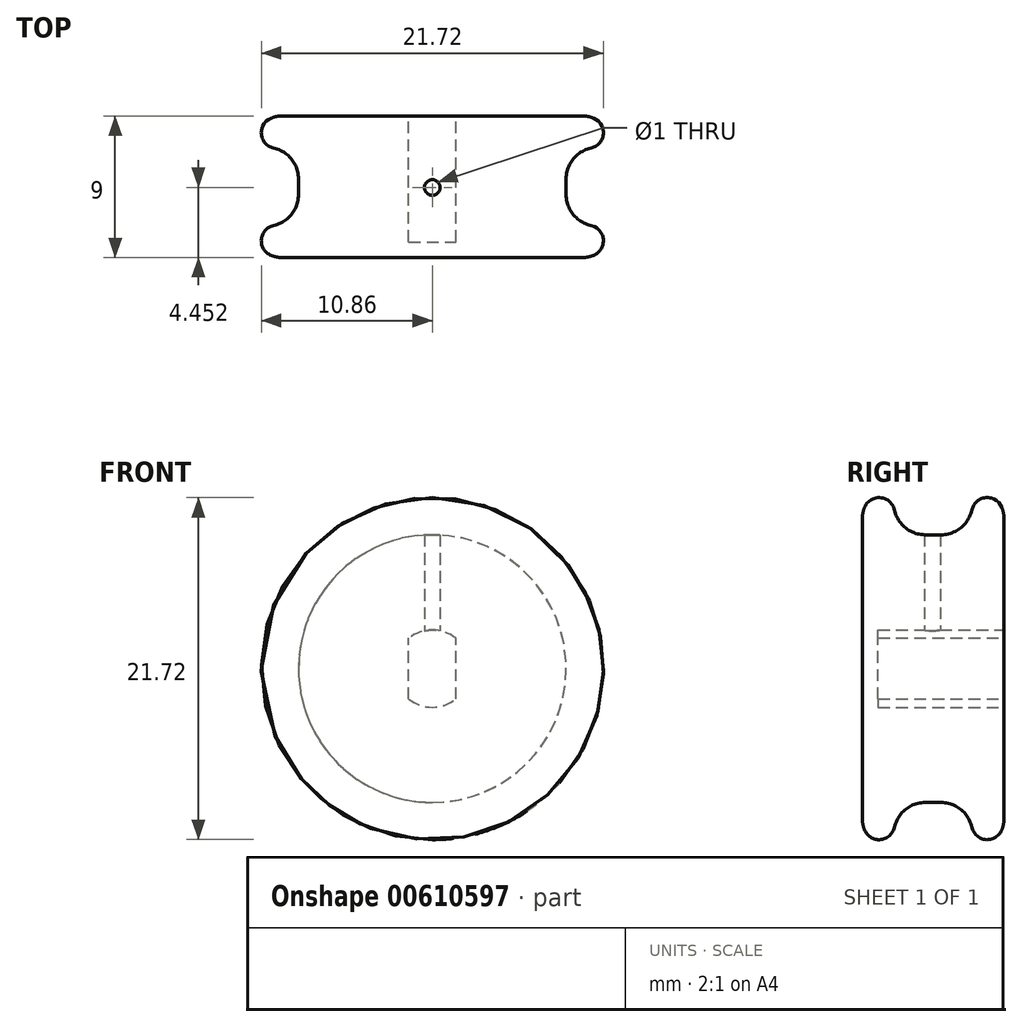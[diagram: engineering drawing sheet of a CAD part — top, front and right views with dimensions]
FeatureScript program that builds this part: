
annotation { "Feature Type Name" : "Feature", "Feature Type Description" : "" }
export const myFeature = defineFeature(function(context is Context, id is Id, definition is map)
    precondition{}
    {
        {
            var Q0;
            Q0=qCreatedBy(makeId("Top.planeOp"),FACE);
            var sketch = newSketch(context, id + "F0", { "sketchPlane" : qUnion([Q0])});
            skLineSegment(sketch, "E0", {"start": v(0, 9) * mm, "end": v(-11.5, 9) * mm});
            skLineSegment(sketch, "E1", {"start": v(-11.5, 9) * mm, "end": v(-11.5, 7) * mm});
            skLineSegment(sketch, "E2", {"start": v(-11.5, 7) * mm, "end": v(-8.5, 7) * mm});
            skLineSegment(sketch, "E3", {"start": v(-8.5, 7) * mm, "end": v(-8.5, 2) * mm});
            skLineSegment(sketch, "E4", {"start": v(-8.5, 2) * mm, "end": v(-11.5, 2) * mm});
            skLineSegment(sketch, "E5", {"start": v(-11.5, 2) * mm, "end": v(-11.5, 0) * mm});
            skLineSegment(sketch, "E6", {"start": v(-11.5, 0) * mm, "end": v(0, 0) * mm});
            skLineSegment(sketch, "E7", {"start": v(0, 9) * mm, "end": v(0, 0) * mm});
            skSolve(sketch);
        }
        {
            var Q0;
            Q0=makeQuery(id+"F0.imprint","IMPRINT",FACE,{"disambiguationData":[TD([[makeQuery(id+"F0.imprint","IMPRINT",EDGE,{"derivedFrom":sQuery(id+"F0.wireOp",EDGE,"E0")}),1.0]])]});
            var Q1;
            Q1=sQuery(id+"F0.wireOp",EDGE,"E7");
            revolve(context, id + "F1", {"entities" : qUnion([Q0]), "axis" : qUnion([Q1]), "revolveType" : RevolveType.FULL});
        }
        {
            var Q0;
            Q0=makeQuery(id+"F1.opRevolve","SWEPT_FACE",FACE,{"disambiguationData":[OSD([sQuery(id+"F0.wireOp",EDGE,"E0")])]});
            var sketch = newSketch(context, id + "F2", { "sketchPlane" : qUnion([Q0])});
            skCircle(sketch, "E8", {"center": v(0, 0) * mm, "radius": 2.45 * mm});
            skLineSegment(sketch, "E9", {"start": v(1.5, -1.94) * mm, "end": v(1.5, 1.94) * mm});
            skLineSegment(sketch, "E10", {"start": v(0, 0) * mm, "end": v(0, 5.78) * mm, "construction": true});
            skLineSegment(sketch, "E11.MirrorCS", {"start": v(-1.5, -1.94) * mm, "end": v(-1.5, 1.94) * mm});
            skSolve(sketch);
        }
        {
            var Q0;
            {var subQ0=sQuery(id+"F2.wireOp",EDGE,"E9");Q0=makeQuery(id+"F2.imprint","IMPRINT",FACE,{"disambiguationData":[TD([[makeQuery(id+"F2.imprint","IMPRINT",EDGE,{"derivedFrom":subQ0}),1.0]])]});}
            extrude(context, id + "F3", {"entities" : qUnion([Q0]), "operationType" : NewBodyOperationType.REMOVE, "oppositeDirection" : true, "depth" : 8 * mm, "offsetDistance" : 25 * mm});
        }
        {
            var Q0;
            Q0=makeQuery(id+"F1.opRevolve","SWEPT_EDGE",EDGE,{"disambiguationData":[OSD([sQuery(id+"F0.wireOp",EDGE,"E2"),sQuery(id+"F0.wireOp",EDGE,"E3")])]});
            var Q1;
            Q1=makeQuery(id+"F1.opRevolve","SWEPT_EDGE",EDGE,{"disambiguationData":[OSD([sQuery(id+"F0.wireOp",EDGE,"E3"),sQuery(id+"F0.wireOp",EDGE,"E4")])]});
            var Q2;
            Q2=makeQuery(id+"F1.opRevolve","SWEPT_EDGE",EDGE,{"disambiguationData":[OSD([sQuery(id+"F0.wireOp",EDGE,"E5"),sQuery(id+"F0.wireOp",EDGE,"E6")])]});
            var Q3;
            Q3=makeQuery(id+"F1.opRevolve","SWEPT_EDGE",EDGE,{"disambiguationData":[OSD([sQuery(id+"F0.wireOp",EDGE,"E0"),sQuery(id+"F0.wireOp",EDGE,"E1")])]});
            fillet(context, id + "F4", {"entities" : qUnion([Q0, Q1, Q2, Q3]), "radius" : 2 * mm, "tangentPropagation" : true, "allowEdgeOverflow" : false});
        }
        {
            var Q0;
            Q0=makeQuery(id+"F4.opFillet","BLEND_EDGE",EDGE,{"blendedFrom":[makeQuery(id+"F1.opRevolve","SWEPT_EDGE",EDGE,{"disambiguationData":[OSD([sQuery(id+"F0.wireOp",EDGE,"E5"),sQuery(id+"F0.wireOp",EDGE,"E6")])]}),makeQuery(id+"F1.opRevolve","SWEPT_FACE",FACE,{"disambiguationData":[OSD([sQuery(id+"F0.wireOp",EDGE,"E4")])]})],"blendedInto":[makeQuery(id+"F1.opRevolve","SWEPT_FACE",FACE,{"disambiguationData":[OSD([sQuery(id+"F0.wireOp",EDGE,"E4")])]})]});
            var Q1;
            Q1=makeQuery(id+"F4.opFillet","BLEND_EDGE",EDGE,{"blendedFrom":[makeQuery(id+"F1.opRevolve","SWEPT_EDGE",EDGE,{"disambiguationData":[OSD([sQuery(id+"F0.wireOp",EDGE,"E0"),sQuery(id+"F0.wireOp",EDGE,"E1")])]}),makeQuery(id+"F1.opRevolve","SWEPT_FACE",FACE,{"disambiguationData":[OSD([sQuery(id+"F0.wireOp",EDGE,"E2")])]})],"blendedInto":[makeQuery(id+"F1.opRevolve","SWEPT_FACE",FACE,{"disambiguationData":[OSD([sQuery(id+"F0.wireOp",EDGE,"E2")])]})]});
            fillet(context, id + "F5", {"entities" : qUnion([Q0, Q1]), "radius" : 1 * mm, "tangentPropagation" : true, "allowEdgeOverflow" : false});
        }
        {
            var Q0;
            Q0=qCreatedBy(makeId("Top.planeOp"),FACE);
            var sketch = newSketch(context, id + "F6", { "sketchPlane" : qUnion([Q0])});
            skPoint(sketch, "E12", {"position": v(0, 4.45) * mm});
            skSolve(sketch);
        }
        {
            var Q0;
            Q0=sQuery(id+"F6.wireOp",VERTEX,"E12");
            var Q1;
            Q1=makeQuery(id+"F1.opRevolve","SWEPT_BODY",BODY,{"disambiguationData":[OSD([sQuery(id+"F0.wireOp",EDGE,"E0"),sQuery(id+"F0.wireOp",EDGE,"E1"),sQuery(id+"F0.wireOp",EDGE,"E2"),sQuery(id+"F0.wireOp",EDGE,"E3"),sQuery(id+"F0.wireOp",EDGE,"E4"),sQuery(id+"F0.wireOp",EDGE,"E5"),sQuery(id+"F0.wireOp",EDGE,"E6"),sQuery(id+"F0.wireOp",EDGE,"E7")])]});
            hole(context, id + "F7", {"style" : HoleStyle.SIMPLE, "endStyle" : HoleEndStyle.THROUGH, "oppositeDirection" : true, "holeDiameter" : 1 * mm, "majorDiameter" : 5 * mm, "isTappedThrough" : true, "tappedDepth" : 12 * mm, "tapClearance" : 3, "locations" : qUnion([Q0]), "scope" : qUnion([Q1])});
        }
    });
